# Revit family: Haworth_Nia_Chair_EU_PRELIMINARY
name_source: partatom
category: Furniture
units: mm (PartAtom-declared; Revit-internal decimal feet)

## family parameters
Always vertical = Yes
Cut with Voids When Loaded = No
OmniClass Number = 23.40.20.00
OmniClass Title = General Furniture and Specialties
Room Calculation Point = No
Shared = No
Work Plane-Based = No

## types (6) — shared parameters
Actual Depth = 68 cm
Actual Width = 68 cm
Assembly Code = E2020200
Caster Finish = Haworth _ Polymer _ Black
Description = Haworth - Nia - Chair - Task
Hardware Finish = Haworth _ Paint _ Black
Manufacturer = Haworth
Model = SENIAX
Plastic Trim Finish = Haworth _ Polymer _ Black
Size = Verify Final Dim. w/ Haworth
URL = https://www.haworth.com
URL - Product = https://www.haworth.com
Version = 1
Warranty = http://www.haworth.com

## per-type parameters (varying)
| type | Actual Height | Fixed Arms | Height Adjustable Arms | High Back | Mid Back | Seat Height | Stool Chair | Task Chair | With Arms | Without Arms |
| High Back - Fixed Arms | 107 cm | Yes | No | Yes | No | 18 cm | Yes | No | Yes | No |
| High Back - Without Arms | 107 cm | No | No | Yes | No | 0 cm | No | Yes | No | Yes |
| Mid Back - Fixed Arms | 101 cm | Yes | No | No | Yes | 0 cm | No | Yes | Yes | No |
| Mid Back - Without Arms | 101 cm | No | No | No | Yes | 18 cm | Yes | No | No | Yes |
| High Back - Height Adjustable Arms | 107 cm | No | Yes | Yes | No | 18 cm | Yes | No | Yes | No |
| Mid Back - Height Adjustable Arms | 101 cm | No | Yes | No | Yes | 0 cm | No | Yes | Yes | No |

## geometry (parser evidence)
native form markers: Sweep x16
no freeform markers — native parametric forms only
